# Revit family: 0052354 Sylvania Lighting Fixture RANA LINEAR R 3KLM NW LOUV+PRI 1-10 WHITE
name_source: partatom
category: Lighting Fixtures
revit_build: Autodesk Revit 2016 (Build: 20150220_1215(x64)
units: mm (PartAtom-declared; Revit-internal decimal feet)

## family parameters
Cut with Voids When Loaded = No
Host = Face
Light Source = Yes
OmniClass Number = 23.80.70.00
OmniClass Title = Lighting
Part Type = Normal
Room Calculation Point = No
Round Connector Dimension = Use Diameter
Shared = No

## types (1)
- 0052354 RANA LINEAR R 3KLM NW LOUV+PRI 1-10
    Apparent Load = 27 VA
    Assembly Code = D5020200
    AssetType = Fixed
    ClassificationName = Uniclass2015
    ClassificationValue = EF_70_80
    Color Filter = 16777215
    Cost = 0 $
    Default Elevation = 1219 mm
    Description = Ceiling recessed LED Linear luminaire with Louvre + Micro Prismatic Optic, Dimensions: 1154mm x 90mm x 91mm, Direct, White Body,  1-10V Dimmable,  Neutral White LED (4000K), 3250lm, 27W, 120lm/W efficacy,  CRI>80, 3 SDCM (3-step MacAdam ellipse), Low LED Flicker (+/-5%), UGR<19, L90B10 at 50,000 hours,  Electric Class1, Glow Wire Test 850°C, Can be covered with building insulation of Glass wool type
    Diffuser_SYL = No
    Dimming Lamp Color Temperature Shift = <None>
    DocumentationLiterature = http://www.sylvania-lighting.com
    ElectricShockClassification = Class I
    Emit Shape Visible in Rendering = No
    Emit from Rectangle Length = 1130 mm  [stored 3.70735 ft]
    Emit from Rectangle Width = 61 mm  [stored 0.200131 ft]
    IfcExportAs = IfcLightFixtureType
    IfcExportType = IfcLightFixtureType
    ImpactProtectionIndex = IK07
    IngressProtection = IP20
    Inset_SYL = 12 mm  [stored 0.0393701 ft]
    Keynote = 16500
    Lamp = LED
    LampColourRenderingIndex = 80
    LampColourTemperature = 4000 K
    LampNominalLuminous = 3250 lm
    LampsType = LED
    Length_SYL = 1154 mm  [stored 3.78609 ft]
    LightOutputRatio = 100
    LouverNumber_SYL = 32
    LouverPrizm_SYL = Yes
    LuminousEfficacy = 120.3 lm/W
    Manufacturer = Feilo Sylvania
    ManufacturerName = Feilo Sylvania
    Material = steel housing, polycarbonate diffuser
    Material_1_SYL = Body-Sylvania-Rana-White
    Material_2_SYL = Diffuser-Sylvania-Rana
    Material_3_SYL = <By Category>
    Material_4_SYL = <By Category>
    Model = RANA LINEAR R 3KLM NW LOUV+PRI 1-10 WHITE
    ModelNumber = 0052354
    ModelReference = RANA LINEAR R 3KLM NW LOUV+PRI 1-10 WHITE
    Name = RANA LINEAR R 3KLM NW LOUV+PRI 1-10 WHITE
    NominalDepth = 90 mm  [stored 0.295276 ft]
    NominalHeight = 91 mm
    NominalLength = 1150 mm
    Photometric Web File = 0052354.ies
    PowerConsumption = 27 W
    PowerFactor = 0
    RecessLength_SYL = 1142 mm  [stored 3.74672 ft]
    RecessWidth_SYL = 72 mm  [stored 0.23622 ft]
    ReflectorLength_SYL = 1130 mm  [stored 3.70735 ft]
    Tilt Angle = -90.00°
    Type Image = <None>
    TypeName = RANA LINEAR R 3KLM NW LOUV+PRI 1-10 WHITE
    URL = http://www.sylvania-lighting.com
    Voltage = 0 V
    Weight = 3.15 kg
    Width_SYL = 90 mm  [stored 0.295276 ft]

note: [stored X ft] marks values corroborated as IEEE doubles in the binary element streams (Revit-internal decimal feet)

## geometry (parser evidence)
native form markers: Sweep x6
no freeform markers — native parametric forms only
